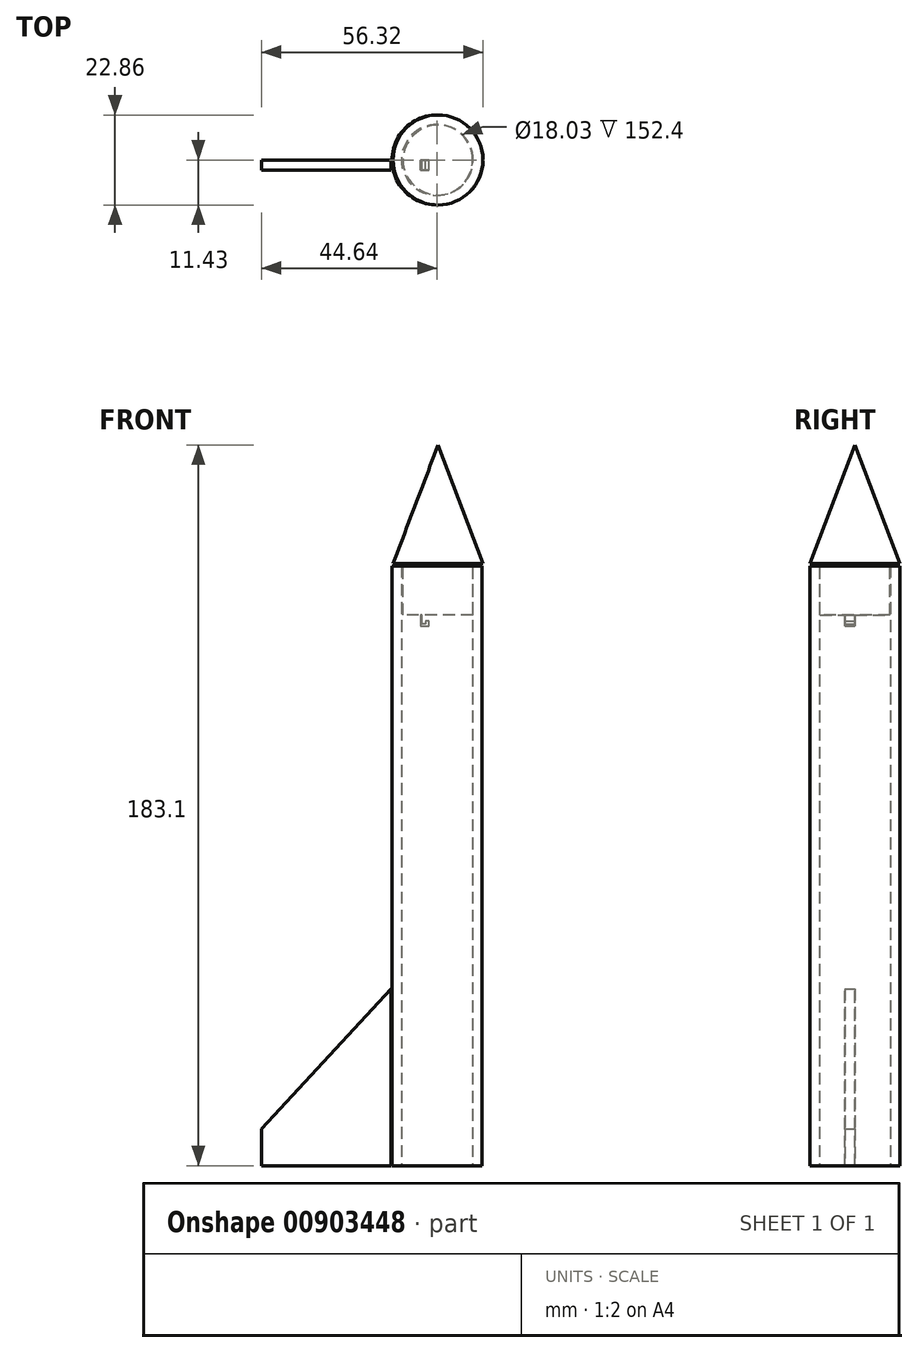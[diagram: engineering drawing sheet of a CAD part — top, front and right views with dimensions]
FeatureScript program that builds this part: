
annotation { "Feature Type Name" : "Feature", "Feature Type Description" : "" }
export const myFeature = defineFeature(function(context is Context, id is Id, definition is map)
    precondition{}
    {
        {
            var Q0;
            Q0=qCreatedBy(makeId("Top.planeOp"),FACE);
            var sketch = newSketch(context, id + "F0", { "sketchPlane" : qUnion([Q0])});
            skCircle(sketch, "E0", {"center": v(0, 0) * mm, "radius": 11.43 * mm});
            skCircle(sketch, "E1", {"center": v(0, 0) * mm, "radius": 9.02 * mm});
            skSolve(sketch);
        }
        {
            var Q0;
            Q0=makeQuery(id+"F0.imprint","IMPRINT",FACE,{"disambiguationData":[TD([[makeQuery(id+"F0.imprint","IMPRINT",EDGE,{"derivedFrom":sQuery(id+"F0.wireOp",EDGE,"E0")}),1.0]])]});
            extrude(context, id + "F1", {"entities" : qUnion([Q0]), "depth" : 152.4 * mm, "offsetDistance" : 25.4 * mm});
        }
        {
            var Q0;
            Q0=qCreatedBy(makeId("Front.planeOp"),FACE);
            var sketch = newSketch(context, id + "F2", { "sketchPlane" : qUnion([Q0])});
            skLineSegment(sketch, "E2", {"start": v(-11.64, 0) * mm, "end": v(-11.64, 44.94) * mm});
            skLineSegment(sketch, "E3", {"start": v(-11.64, 44.94) * mm, "end": v(-44.64, 9.4) * mm});
            skLineSegment(sketch, "E4", {"start": v(-44.64, 9.4) * mm, "end": v(-44.64, 0) * mm});
            skLineSegment(sketch, "E5", {"start": v(-44.64, 0) * mm, "end": v(-11.64, 0) * mm});
            skSolve(sketch);
        }
        {
            var Q0;
            Q0=makeQuery(id+"F2.imprint","IMPRINT",FACE,{"disambiguationData":[TD([[makeQuery(id+"F2.imprint","IMPRINT",EDGE,{"derivedFrom":sQuery(id+"F2.wireOp",EDGE,"E2")}),1.0]])]});
            extrude(context, id + "F3", {"entities" : qUnion([Q0]), "depth" : 2.54 * mm, "offsetDistance" : 25.4 * mm});
        }
        {
            var Q0;
            Q0=qCreatedBy(makeId("Front.planeOp"),FACE);
            var sketch = newSketch(context, id + "F4", { "sketchPlane" : qUnion([Q0])});
            skLineSegment(sketch, "E6", {"start": v(0.25, 183.1) * mm, "end": v(0.25, 139.89) * mm});
            skLineSegment(sketch, "E7", {"start": v(0.25, 139.89) * mm, "end": v(-8.64, 139.89) * mm});
            skLineSegment(sketch, "E8", {"start": v(-8.64, 139.89) * mm, "end": v(-8.64, 152.94) * mm});
            skLineSegment(sketch, "E9", {"start": v(-8.64, 152.94) * mm, "end": v(-11.18, 152.94) * mm});
            skLineSegment(sketch, "E10", {"start": v(-11.18, 152.94) * mm, "end": v(0.25, 183.1) * mm});
            skLineSegment(sketch, "E11", {"start": v(-4.2, 139.89) * mm, "end": v(-4.2, 137.05) * mm});
            skLineSegment(sketch, "E12", {"start": v(-4.2, 137.05) * mm, "end": v(-2, 137.05) * mm});
            skLineSegment(sketch, "E13", {"start": v(-2, 137.05) * mm, "end": v(-2, 138.38) * mm});
            skLineSegment(sketch, "E14", {"start": v(-2, 138.38) * mm, "end": v(-2.88, 138.38) * mm});
            skLineSegment(sketch, "E15", {"start": v(-2.88, 138.38) * mm, "end": v(-2.88, 137.6) * mm});
            skLineSegment(sketch, "E16", {"start": v(-2.88, 137.6) * mm, "end": v(-3.78, 137.6) * mm});
            skLineSegment(sketch, "E17", {"start": v(-3.78, 137.6) * mm, "end": v(-3.78, 139.89) * mm});
            skSolve(sketch);
        }
        {
            var Q0;
            Q0=makeQuery(id+"F4.imprint","IMPRINT",FACE,{"disambiguationData":[TD([[makeQuery(id+"F4.imprint","IMPRINT",EDGE,{"derivedFrom":sQuery(id+"F4.wireOp",EDGE,"E6")}),-1.0]])]});
            var Q1;
            Q1=sQuery(id+"F4.wireOp",EDGE,"E6");
            revolve(context, id + "F5", {"surfaceOperationType" : NewSurfaceOperationType.NEW, "entities" : qUnion([Q0]), "axis" : qUnion([Q1]), "revolveType" : RevolveType.FULL});
        }
        {
            var Q0;
            {var subQ0=sQuery(id+"F4.wireOp",EDGE,"E11");Q0=makeQuery(id+"F4.imprint","IMPRINT",FACE,{"disambiguationData":[TD([[makeQuery(id+"F4.imprint","IMPRINT",EDGE,{"derivedFrom":subQ0}),1.0]])]});}
            extrude(context, id + "F6", {"entities" : qUnion([Q0]), "operationType" : NewBodyOperationType.ADD, "depth" : 2.54 * mm, "offsetDistance" : 25.4 * mm});
        }
    });
